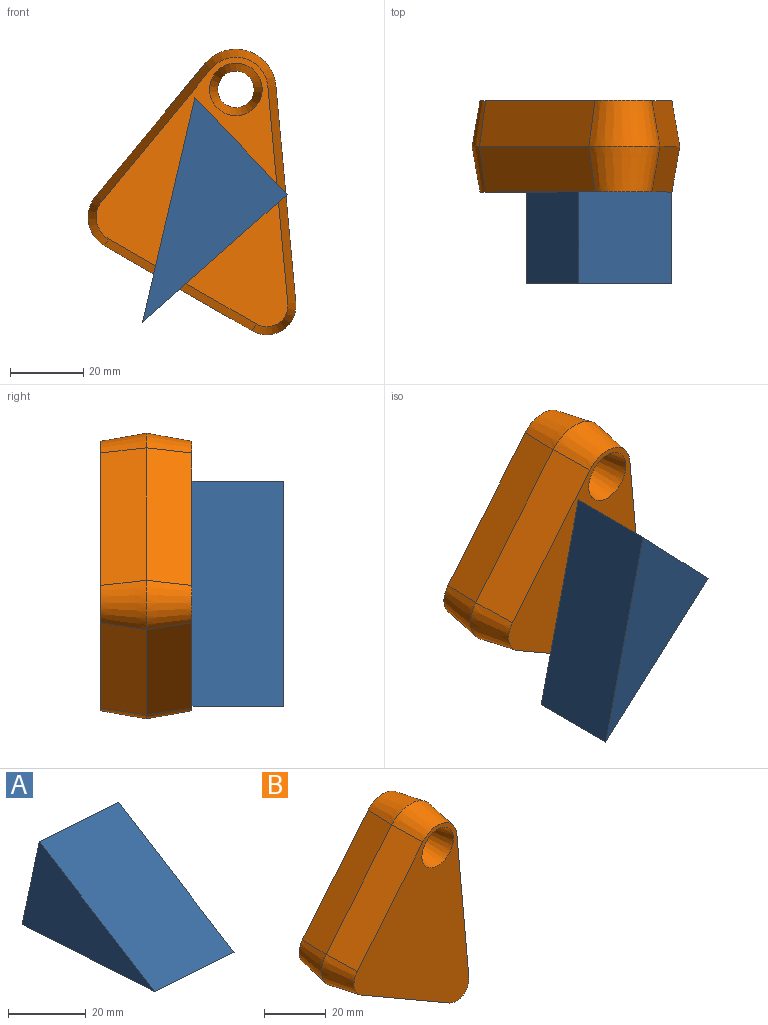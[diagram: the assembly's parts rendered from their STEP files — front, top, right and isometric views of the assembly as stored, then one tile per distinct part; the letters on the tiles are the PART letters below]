
ASSEMBLY  parts=2 mates=1
PART A: 5 faces, bbox 36.5x64.5x36.6 mm
  f0: plane 36.63x29.71mm, normal (0.13,0.93,0.33), area 915.4mm2, adj f1,f2,f3,f4
  f1: plane 53.02x31.36mm, normal (-0.15,-0.35,0.93), area 1320.9mm2, adj f0,f2,f3,f4
  f2: plane 64.52x36.55mm, normal (0.04,-0.25,-0.97), area 1579.4mm2, adj f0,f1,f3,f4
  f3: plane 60.17x34.38mm, normal (0.98,-0.17,0.09), area 966.7mm2, adj f0,f1,f2
  f4: plane 60.17x34.38mm, normal (-0.98,0.17,-0.09), area 966.7mm2, adj f0,f1,f2
PART B: 16 faces, bbox 56.9x25x78.2 mm
  f0: cone r=5mm half-angle=10deg, axis (0,-1,0), area 486.6mm2, adj f1,f13
  f1: plane 73.8x52.51mm, normal (0,-1,0), area 2180.8mm2, adj f0,f2,f3,f4,f5,f6,f7
  f2: cone r=8mm half-angle=10deg, axis (0,1,0), area 191.4mm2, adj f1,f3,f7,f14
  f3: plane 41.52x25.24mm, normal (-0.49,-0.17,-0.85), area 592.4mm2, adj f1,f2,f4,f12
  f4: cone r=9mm half-angle=10deg, axis (0,1,0), area 174.1mm2, adj f1,f3,f5,f11
  f5: plane 37.68x31.63mm, normal (-0.76,-0.17,0.63), area 596.9mm2, adj f1,f4,f6,f10
  f6: cone r=11mm half-angle=10deg, axis (0,1,0), area 296.5mm2, adj f1,f5,f7,f9
  f7: plane 59.68x12.5mm, normal (0.98,-0.17,0.09), area 758.2mm2, adj f1,f2,f6,f8
  f8: plane 59.68x12.5mm, normal (0.98,0.17,0.09), area 758.2mm2, adj f7,f9,f14,f15
  f9: cone r=11mm half-angle=10deg, axis (0,-1,0), area 296.5mm2, adj f6,f8,f10,f15
  f10: plane 37.68x31.63mm, normal (-0.76,0.17,0.63), area 596.9mm2, adj f5,f9,f11,f15
  f11: cone r=9mm half-angle=10deg, axis (0,-1,0), area 174.1mm2, adj f4,f10,f12,f15
  f12: plane 41.52x25.24mm, normal (-0.49,0.17,-0.85), area 592.4mm2, adj f3,f11,f14,f15
  f13: cone r=5mm half-angle=10deg, axis (0,1,0), area 486.6mm2, adj f0,f15
  f14: cone r=8mm half-angle=10deg, axis (0,-1,0), area 191.4mm2, adj f2,f8,f12,f15
  f15: plane 73.8x52.51mm, normal (0,1,0), area 2180.8mm2, adj f8,f9,f10,f11,f12,f13,f14
PLACE A rot(axis=(0.67,0.59,0.45),144.3deg) t=(-66.65,-54.25,18.52)mm
PLACE B t=(-25.63,-22.38,9.45)mm
MATE parallel A.f3 <-> B.f1  axis (0,1,0) through (-53.21,-34.88,12.89)mm
